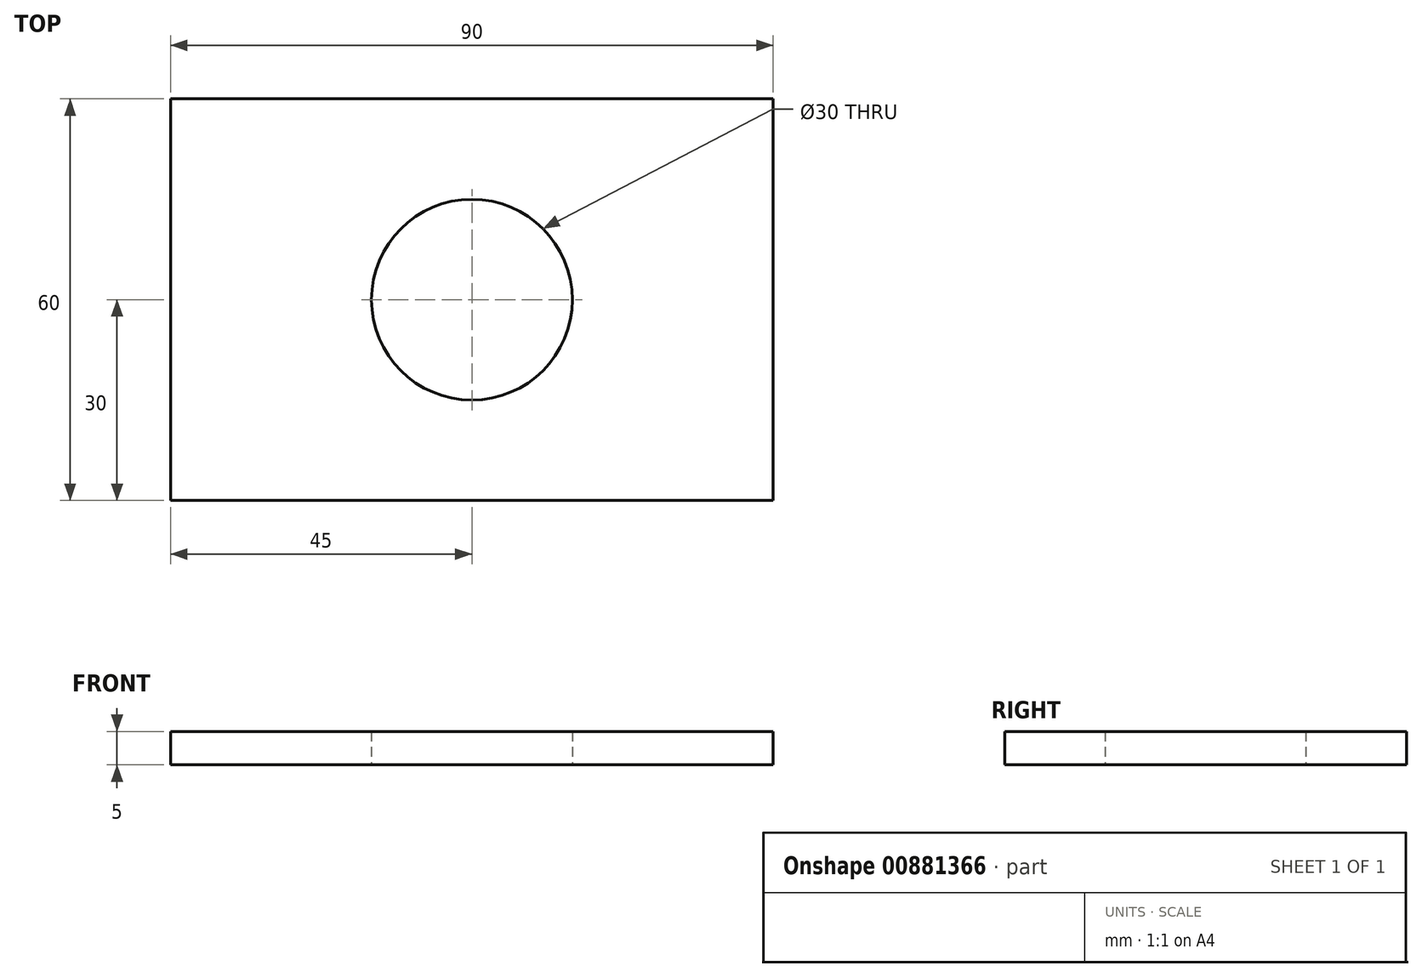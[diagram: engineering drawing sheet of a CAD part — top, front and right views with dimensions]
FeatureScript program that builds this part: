
annotation { "Feature Type Name" : "Feature", "Feature Type Description" : "" }
export const myFeature = defineFeature(function(context is Context, id is Id, definition is map)
    precondition{}
    {
        {
            var Q0;
            Q0=qCreatedBy(makeId("Top.planeOp"),FACE);
            var sketch = newSketch(context, id + "F0", { "sketchPlane" : qUnion([Q0])});
            skLineSegment(sketch, "E0.bottom", {"start": v(45, 30) * mm, "end": v(-45, 30) * mm});
            skLineSegment(sketch, "E0.top", {"start": v(45, -30) * mm, "end": v(-45, -30) * mm});
            skLineSegment(sketch, "E0.left", {"start": v(45, 30) * mm, "end": v(45, -30) * mm});
            skLineSegment(sketch, "E0.right", {"start": v(-45, 30) * mm, "end": v(-45, -30) * mm});
            skPoint(sketch, "E0.middle", {"position": v(0, 0) * mm});
            skCircle(sketch, "E1", {"center": v(0, 0) * mm, "radius": 15 * mm});
            skSolve(sketch);
        }
        {
            var Q0;
            Q0=makeQuery(id+"F0.imprint","IMPRINT",FACE,{"disambiguationData":[TD([[makeQuery(id+"F0.imprint","IMPRINT",EDGE,{"derivedFrom":sQuery(id+"F0.wireOp",EDGE,"E0.bottom")}),1.0]])]});
            extrude(context, id + "F1", {"entities" : qUnion([Q0]), "depth" : 5 * mm, "offsetDistance" : 25 * mm});
        }
    });
